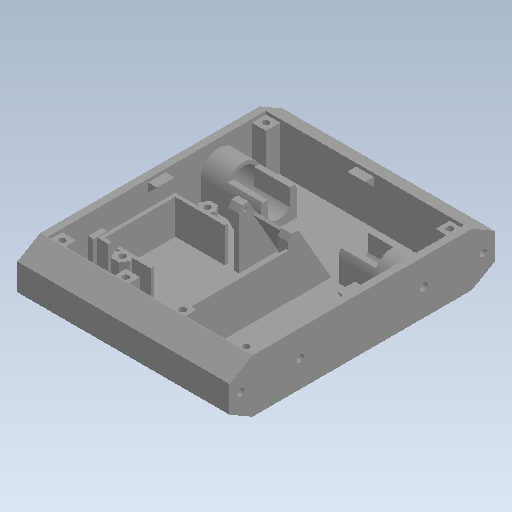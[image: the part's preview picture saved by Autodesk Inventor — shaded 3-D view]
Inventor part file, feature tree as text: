
AUTODESK INVENTOR PART (.ipt)
format: ipt  version: 2020 (Build 240168000, 168)  size: 724,480 bytes
history: native  units: in
note: dims shown in document units (in); Inventor stores cm internally (conversion verified against a paired STEP export)
features: extrude x21, sketch x21, projected_geometry x16, mirror x7, plane x1
ambient origin geometry x8: Origin, YZ Plane, XZ Plane, XY Plane, X Axis, Y Axis, Z Axis, Center Point
bodies: Solid1 (feature_tree)
feature tree (66):
  extrude  "Extrusion1"  Depth=5.9055in
  extrude  "Extrusion2"  TaperAngle=0.0deg  [1 undecoded]
  extrude  "Extrusion3"  Depth=1.063in
  extrude  "Extrusion4"  Depth=0.315in
  extrude  "Extrusion5"  TaperAngle=0.0deg  [1 undecoded]
  extrude  "Extrusion6"  Depth=0.5906in
  mirror  "Mirror1"
  extrude  "Extrusion7"  Depth=0.0787in
  mirror  "Mirror2"
  extrude  "Extrusion8"  Depth=0.6102in
  mirror  "Mirror3"
  plane  "Work Plane1"
  extrude  "Extrusion9"  Depth=0.7874in TaperAngle=0.0deg
  mirror  "Mirror4"
  extrude  "Extrusion10"  Depth=6.063in TaperAngle=0.0deg
  extrude  "Extrusion11"  Depth=0.1575in
  extrude  "Extrusion12"  TaperAngle=0.0deg  [1 undecoded]
  extrude  "Extrusion13"  Depth=0.2756in
  extrude  "Extrusion14"  Depth=0.4331in
  extrude  "Extrusion17"  Depth=2.7559in
  extrude  "Extrusion18"  Depth=0.0453in
  mirror  "Mirror6"
  extrude  "Extrusion19"  TaperAngle=0.0deg  [1 undecoded]
  mirror  "Mirror7"
  extrude  "Extrusion20"  Depth=0.0787in
  extrude  "Extrusion21"  Depth=0.993in
  extrude  "Extrusion22"  Depth=0.2756in
  extrude  "Extrusion23"  Depth=0.4724in
  mirror  "Mirror8"
  sketch  "Sketch1"  dims[d0=1.1811in d1=5.9055in]
  sketch  "Sketch2"  dims[d2=4.7244in d3=0.0in]
  projected_geometry  "Projected Loop1"
  sketch  "Sketch3"  dims[d4=0.1575in d5=1.063in]
  projected_geometry  "Projected Loop2"
  projected_geometry  "Projected Loop3"
  sketch  "Sketch4"  dims[d6=0.0in d8=0.315in]
  sketch  "Sketch5"  dims[d10=0.993in d11=0.0in]
  projected_geometry  "Projected Loop4"
  sketch  "Sketch6"  dims[d12=0.6496in d13=0.5906in]
  sketch  "Sketch7"  dims[d14=1.5748in d15=0.0787in]
  sketch  "Sketch9"  dims[d16=0.5512in d17=0.0in d18=0.6102in]
  sketch  "Sketch10"  dims[d19=0.4803in d20=0.7874in d21=0.0in]
  sketch  "Sketch12"  dims[d22=0.1654in d23=6.063in d24=0.0in]
  projected_geometry  "Projected Loop6"
  projected_geometry  "Projected Loop7"
  projected_geometry  "Projected Loop8"
  sketch  "Sketch13"  dims[d25=0.5114in d26=0.1575in]
  sketch  "Sketch14"  dims[d27=1.5748in d28=0.0in d29=0.0in]
  sketch  "Sketch15"  dims[d30=0.1575in d31=0.2756in]
  projected_geometry  "Projected Loop15"
  sketch  "Sketch16"  dims[d32=0.0in d33=0.4331in]
  projected_geometry  "Projected Loop19"
  projected_geometry  "Projected Loop20"
  projected_geometry  "Projected Loop21"
  projected_geometry  "Projected Loop22"
  projected_geometry  "Projected Loop23"
  projected_geometry  "Projected Loop24"
  sketch  "Sketch20"  dims[d34=0.0906in d38=2.7559in]
  sketch  "Sketch21"  dims[d40=0.0453in d41=0.0909in]
  sketch  "Sketch22"  dims[d42=0.2362in d43=0.0in]
  sketch  "Sketch23"  dims[d44=60.0deg d45=0.0787in]
  sketch  "Sketch25"  dims[d46=0.315in d48=0.993in]
  sketch  "Sketch26"  dims[d49=0.0in d53=0.2756in]
  projected_geometry  "Projected Loop25"
  sketch  "Sketch27"  dims[d54=0.0in d55=0.4724in d56=1.1811in d57=1.5748in d58=1.5748in d59=0.0787in d60=0.0787in d62=0.315in d63=0.7677in d64=0.0in d66=0.1476in d67=0.2756in d68=0.0in d69=0.7874in d70=0.2953in d71=0.1181in d72=0.0in d89=0.0157in d90=0.0157in d91=0.1476in d92=0.1476in d96=0.315in d97=0.1575in d98=0.1181in d99=0.0in d102=0.1772in d104=0.3346in d105=135.0deg d106=0.2362in d107=0.0in d108=0.0394in d109=0.0in d110=0.063in d111=0.0394in d112=0.0in d117=0.993in d118=0.063in d119=0.3937in d120=0.0in d121=45.0deg d122=0.993in d123=0.1969in d124=0.3937in d125=0.0in d126=45.0deg d127=0.1969in d128=0.993in d129=0.3937in d130=0.0in]
  projected_geometry  "Projected Loop26"
note: 4 required parameter values undecoded (feature->parameter linkage not recoverable at this tier; creation-order binding heuristic only, values carry confidence <= 0.55)
